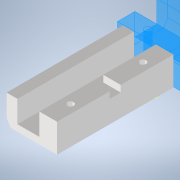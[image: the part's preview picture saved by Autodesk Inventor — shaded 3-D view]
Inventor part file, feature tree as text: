
AUTODESK INVENTOR PART (.ipt)
format: ipt  version: 2021 (Build 250183000, 183)  size: 154,112 bytes
history: native  units: mm
features: sketch x7, extrude x6, other x1
ambient origin geometry x8: Origin, YZ Plane, XZ Plane, XY Plane, X Axis, Y Axis, Z Axis, Center Point
bodies: Body1 (feature_tree)
feature tree (14):
  other  "Sólido1"
  extrude  "Extrusión1"  Depth=53.0mm
  extrude  "Extrusión2"  Depth=8.0mm
  extrude  "Extrusión3"  Depth=24.0mm
  extrude  "Extrusión4"  Depth=24.0mm
  extrude  "Extrusión5"  Depth=3.0mm
  extrude  "Extrusión7"  Depth=10.0mm
  sketch  "Boceto8"  dims[d15=14.75mm d16=0.0mm d17=5.0mm d18=10.0mm d19=0.0mm d24=2.0mm d25=3.0mm d26=55.5mm d27=0.0mm]
  sketch  "Boceto1"  dims[d0=23.0mm d1=53.0mm]
  sketch  "Boceto2"  dims[d2=3.0mm d3=0.0mm d4=8.0mm]
  sketch  "Boceto3"  dims[d5=10.0mm d6=0.0mm d7=24.0mm]
  sketch  "Boceto4"  dims[d8=5.0mm d9=24.0mm]
  sketch  "Boceto5"  dims[d10=3.0mm d11=0.0mm d12=3.0mm]
  sketch  "Boceto7"  dims[d13=10.0mm d14=4.0mm]
